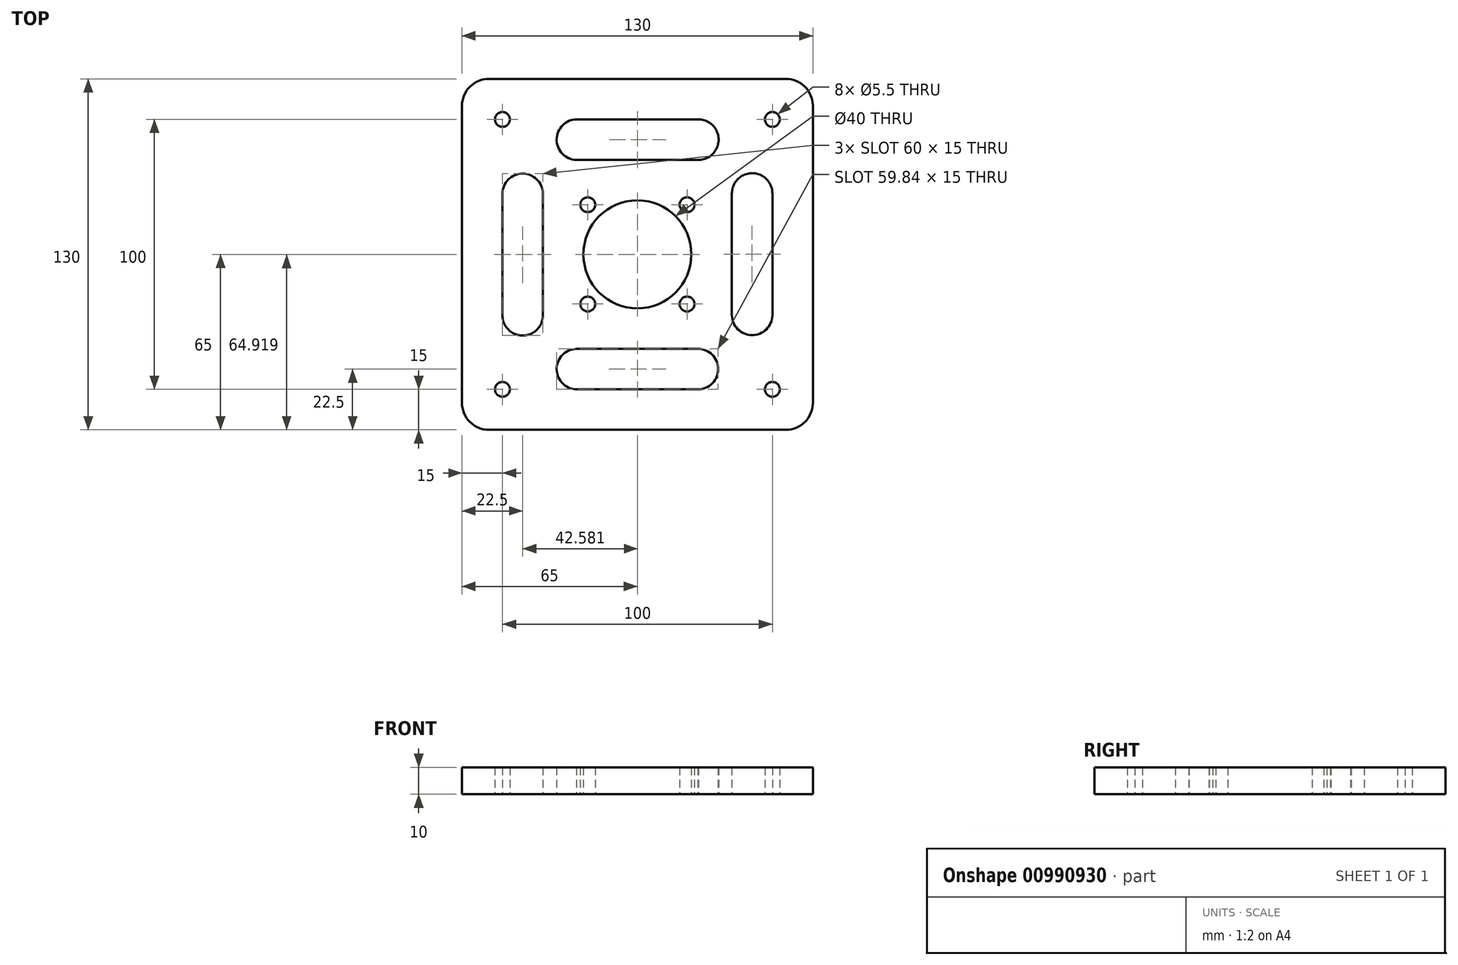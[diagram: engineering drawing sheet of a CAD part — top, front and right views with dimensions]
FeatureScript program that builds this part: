
annotation { "Feature Type Name" : "Feature", "Feature Type Description" : "" }
export const myFeature = defineFeature(function(context is Context, id is Id, definition is map)
    precondition{}
    {
        {
            var Q0;
            Q0=qCreatedBy(makeId("Top.planeOp"),FACE);
            var sketch = newSketch(context, id + "F0", { "sketchPlane" : qUnion([Q0])});
            skLineSegment(sketch, "E0.bottom", {"start": v(55, -65) * mm, "end": v(-55, -65) * mm});
            skLineSegment(sketch, "E0.top", {"start": v(55, 65) * mm, "end": v(-55, 65) * mm});
            skLineSegment(sketch, "E0.left", {"start": v(65, -55) * mm, "end": v(65, 55) * mm});
            skLineSegment(sketch, "E0.right", {"start": v(-65, -55) * mm, "end": v(-65, 55) * mm});
            skPoint(sketch, "E0.middle", {"position": v(0, 0) * mm});
            skCircle(sketch, "E1", {"center": v(0, 0) * mm, "radius": 20 * mm});
            skLineSegment(sketch, "E2", {"start": v(20, 0) * mm, "end": v(65, 0) * mm, "construction": true});
            skLineSegment(sketch, "E3", {"start": v(0, -20) * mm, "end": v(0, -65) * mm, "construction": true});
            skCircle(sketch, "E4", {"center": v(-50, 50) * mm, "radius": 2.75 * mm});
            skCircle(sketch, "E5.MirrorC", {"center": v(50, 50) * mm, "radius": 2.75 * mm});
            skCircle(sketch, "E6.MirrorC", {"center": v(-50, -50) * mm, "radius": 2.75 * mm});
            skCircle(sketch, "E7.MirrorC", {"center": v(50, -50) * mm, "radius": 2.75 * mm});
            skCircle(sketch, "E8", {"center": v(-18.38, 18.38) * mm, "radius": 2.75 * mm});
            skCircle(sketch, "E9.MirrorC", {"center": v(18.38, 18.38) * mm, "radius": 2.75 * mm});
            skCircle(sketch, "E10.MirrorC", {"center": v(-18.38, -18.38) * mm, "radius": 2.75 * mm});
            skCircle(sketch, "E11.MirrorC", {"center": v(18.38, -18.38) * mm, "radius": 2.75 * mm});
            skCircle(sketch, "E12", {"center": v(0, 0) * mm, "radius": 26 * mm, "construction": true});
            skLineSegment(sketch, "E13.left", {"start": v(-35, -22.42) * mm, "end": v(-35, 22.58) * mm});
            skLineSegment(sketch, "E13.right", {"start": v(-50, -22.58) * mm, "end": v(-50, 22.42) * mm});
            skPoint(sketch, "E13.middle", {"position": v(-42.5, 0) * mm});
            skLineSegment(sketch, "E14.MirrorCS", {"start": v(50, -22.58) * mm, "end": v(50, 22.42) * mm});
            skLineSegment(sketch, "E15.MirrorCS", {"start": v(35, -22.42) * mm, "end": v(35, 22.58) * mm});
            skLineSegment(sketch, "E16", {"start": v(-65, 65) * mm, "end": v(65, -65) * mm, "construction": true});
            skLineSegment(sketch, "E17.MirrorCS", {"start": v(22.42, -35) * mm, "end": v(-22.58, -35) * mm});
            skLineSegment(sketch, "E18.MirrorCS", {"start": v(22.58, -50) * mm, "end": v(-22.42, -50) * mm});
            skLineSegment(sketch, "E19.MirrorCS", {"start": v(22.42, 35) * mm, "end": v(-22.58, 35) * mm});
            skLineSegment(sketch, "E20.MirrorCS", {"start": v(22.58, 50) * mm, "end": v(-22.42, 50) * mm});
            skPoint(sketch, "E21.visualSharp", {"position": v(-65, 65) * mm});
            skArc(sketch, "E21.filletArc", {"start": v(-55, 65) * mm, "mid": v(-62.07, 62.07) * mm, "end": v(-65, 55) * mm});
            skPoint(sketch, "E22.visualSharp", {"position": v(65, 65) * mm});
            skArc(sketch, "E22.filletArc", {"start": v(65, 55) * mm, "mid": v(62.07, 62.07) * mm, "end": v(55, 65) * mm});
            skPoint(sketch, "E23.visualSharp", {"position": v(-65, -65) * mm});
            skArc(sketch, "E23.filletArc", {"start": v(-65, -55) * mm, "mid": v(-62.07, -62.07) * mm, "end": v(-55, -65) * mm});
            skPoint(sketch, "E24.visualSharp", {"position": v(65, -65) * mm});
            skArc(sketch, "E24.filletArc", {"start": v(55, -65) * mm, "mid": v(62.07, -62.07) * mm, "end": v(65, -55) * mm});
            skArc(sketch, "E25", {"start": v(-35, 22.58) * mm, "mid": v(-42.58, 29.92) * mm, "end": v(-50, 22.42) * mm});
            skArc(sketch, "E26", {"start": v(-50, -22.58) * mm, "mid": v(-42.42, -30.08) * mm, "end": v(-35, -22.42) * mm});
            skArc(sketch, "E27", {"start": v(-22.58, -35) * mm, "mid": v(-29.92, -42.58) * mm, "end": v(-22.42, -50) * mm});
            skArc(sketch, "E28", {"start": v(22.58, -50) * mm, "mid": v(29.92, -42.42) * mm, "end": v(22.42, -35) * mm});
            skArc(sketch, "E29", {"start": v(35, -22.42) * mm, "mid": v(42.42, -29.92) * mm, "end": v(50, -22.58) * mm});
            skArc(sketch, "E30", {"start": v(50, 22.42) * mm, "mid": v(42.58, 30.08) * mm, "end": v(35, 22.58) * mm});
            skArc(sketch, "E31", {"start": v(22.42, 35) * mm, "mid": v(30.08, 42.42) * mm, "end": v(22.58, 50) * mm});
            skArc(sketch, "E32", {"start": v(-22.42, 50) * mm, "mid": v(-29.92, 42.58) * mm, "end": v(-22.58, 35) * mm});
            skPoint(sketch, "E33.orphan", {"position": v(-22.58, -35) * mm});
            skPoint(sketch, "E34.orphan", {"position": v(22.42, -35) * mm});
            skPoint(sketch, "E35.orphan", {"position": v(50, -22.58) * mm});
            skPoint(sketch, "E36.MirrorCS.start.orphan", {"position": v(35, -22.42) * mm});
            skPoint(sketch, "E37.orphan", {"position": v(22.58, 50) * mm});
            skPoint(sketch, "E38.MirrorCS.start.orphan", {"position": v(22.42, 35) * mm});
            skPoint(sketch, "E39.orphan", {"position": v(-22.42, 50) * mm});
            skPoint(sketch, "E40.MirrorCS.start.orphan", {"position": v(-22.58, 35) * mm});
            skPoint(sketch, "E41", {"position": v(0.08, 50) * mm});
            skSolve(sketch);
        }
        {
            var Q0;
            Q0 = qSketchRegion(id + "F0", true);
            extrude(context, id + "F1", {"entities" : qUnion([Q0]), "depth" : 10 * mm, "offsetDistance" : 25 * mm});
        }
    });
